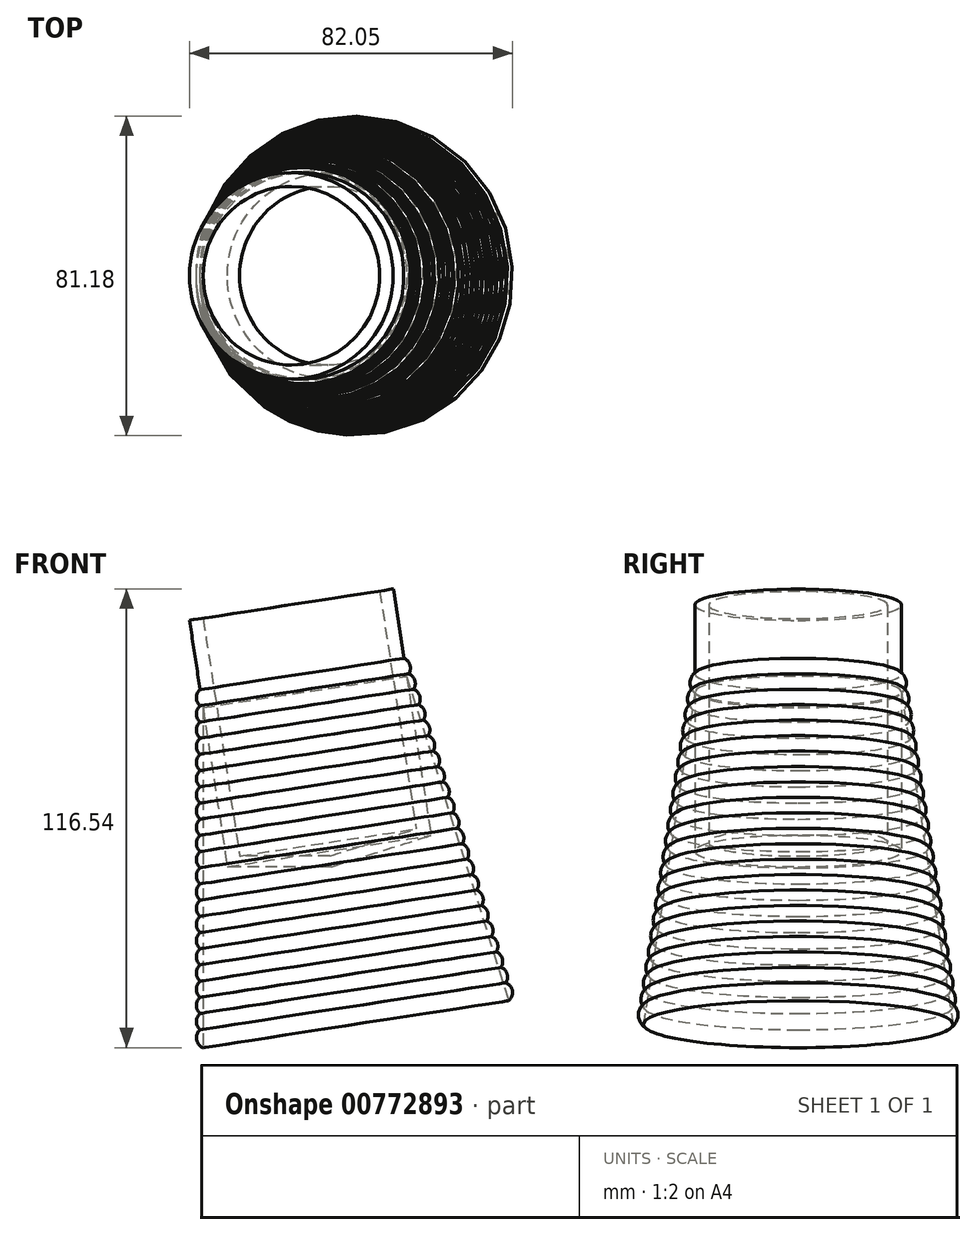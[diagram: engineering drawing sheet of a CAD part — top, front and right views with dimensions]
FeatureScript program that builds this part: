
annotation { "Feature Type Name" : "Feature", "Feature Type Description" : "" }
export const myFeature = defineFeature(function(context is Context, id is Id, definition is map)
    precondition{}
    {
        {
            var Q0;
            Q0=qCreatedBy(makeId("Front.planeOp"),FACE);
            var sketch = newSketch(context, id + "F0", { "sketchPlane" : qUnion([Q0])});
            skLineSegment(sketch, "E0", {"start": v(-26.5, -27.93) * mm, "end": v(-36.1, 34.68) * mm});
            skLineSegment(sketch, "E1", {"start": v(-26.5, -27.93) * mm, "end": v(0, -27.93) * mm});
            skLineSegment(sketch, "E2", {"start": v(0, -27.93) * mm, "end": v(-0.42, -25.21) * mm});
            skLineSegment(sketch, "E3", {"start": v(-0.42, -25.21) * mm, "end": v(-23.38, -25.21) * mm});
            skLineSegment(sketch, "E4", {"start": v(-23.38, -25.21) * mm, "end": v(-32.64, 35.1) * mm});
            skLineSegment(sketch, "E5", {"start": v(-32.64, 35.1) * mm, "end": v(-36.1, 34.68) * mm});
            skArc(sketch, "E6", {"start": v(-33.4, 17.07) * mm, "mid": v(-34.32, 14.6) * mm, "end": v(-32.7, 12.5) * mm});
            skArc(sketch, "E7.0.1.0", {"start": v(-33.4, 12.95) * mm, "mid": v(-34.32, 10.48) * mm, "end": v(-32.7, 8.39) * mm});
            skArc(sketch, "E7.0.2.0", {"start": v(-33.4, 8.84) * mm, "mid": v(-34.32, 6.36) * mm, "end": v(-32.7, 4.27) * mm});
            skArc(sketch, "E7.0.3.0", {"start": v(-33.4, 4.73) * mm, "mid": v(-34.32, 2.25) * mm, "end": v(-32.7, 0.16) * mm});
            skArc(sketch, "E7.0.4.0", {"start": v(-33.4, 0.61) * mm, "mid": v(-34.32, -1.87) * mm, "end": v(-32.7, -3.96) * mm});
            skArc(sketch, "E7.0.5.0", {"start": v(-33.4, -3.5) * mm, "mid": v(-34.32, -5.98) * mm, "end": v(-32.7, -8.07) * mm});
            skArc(sketch, "E7.0.6.0", {"start": v(-33.4, -7.62) * mm, "mid": v(-34.32, -10.1) * mm, "end": v(-32.7, -12.19) * mm});
            skArc(sketch, "E7.0.7.0", {"start": v(-33.4, -11.73) * mm, "mid": v(-34.32, -14.21) * mm, "end": v(-32.7, -16.3) * mm});
            skArc(sketch, "E7.0.8.0", {"start": v(-33.4, -15.85) * mm, "mid": v(-34.32, -18.33) * mm, "end": v(-32.7, -20.42) * mm});
            skArc(sketch, "E7.0.9.0", {"start": v(-33.4, -19.96) * mm, "mid": v(-34.32, -22.44) * mm, "end": v(-32.7, -24.53) * mm});
            skArc(sketch, "E7.0.10.0", {"start": v(-33.4, -24.08) * mm, "mid": v(-34.32, -26.56) * mm, "end": v(-32.7, -28.65) * mm});
            skArc(sketch, "E7.0.11.0", {"start": v(-33.4, -28.2) * mm, "mid": v(-34.32, -30.67) * mm, "end": v(-32.7, -32.76) * mm});
            skArc(sketch, "E7.0.12.0", {"start": v(-33.4, -32.3) * mm, "mid": v(-34.32, -34.79) * mm, "end": v(-32.7, -36.88) * mm});
            skArc(sketch, "E7.0.13.0", {"start": v(-33.4, -36.42) * mm, "mid": v(-34.32, -38.9) * mm, "end": v(-32.7, -41) * mm});
            skArc(sketch, "E7.0.14.0", {"start": v(-33.4, -40.54) * mm, "mid": v(-34.32, -43.02) * mm, "end": v(-32.7, -45.1) * mm});
            skArc(sketch, "E7.0.15.0", {"start": v(-33.4, -44.65) * mm, "mid": v(-34.32, -47.13) * mm, "end": v(-32.7, -49.22) * mm});
            skArc(sketch, "E7.0.16.0", {"start": v(-33.4, -48.77) * mm, "mid": v(-34.32, -51.25) * mm, "end": v(-32.7, -53.34) * mm});
            skArc(sketch, "E7.0.17.0", {"start": v(-33.4, -52.88) * mm, "mid": v(-34.32, -55.36) * mm, "end": v(-32.7, -57.45) * mm});
            skArc(sketch, "E7.0.18.0", {"start": v(-33.4, -57) * mm, "mid": v(-34.32, -59.48) * mm, "end": v(-32.7, -61.56) * mm});
            skArc(sketch, "E7.0.19.0", {"start": v(-33.4, -61.11) * mm, "mid": v(-34.32, -63.6) * mm, "end": v(-32.7, -65.68) * mm});
            skArc(sketch, "E7.0.20.0", {"start": v(-33.4, -65.23) * mm, "mid": v(-34.32, -67.7) * mm, "end": v(-32.7, -69.8) * mm});
            skArc(sketch, "E7.0.21.0", {"start": v(-33.4, -69.34) * mm, "mid": v(-34.32, -71.82) * mm, "end": v(-32.7, -73.9) * mm});
            skLineSegment(sketch, "E7.direction1", {"start": v(-32.7, 12.5) * mm, "end": v(-32.7, 12.5) * mm});
            skLineSegment(sketch, "E7.direction2", {"start": v(-32.7, 12.5) * mm, "end": v(-32.7, 8.39) * mm, "construction": true});
            skLineSegment(sketch, "E8", {"start": v(-32.7, 12.5) * mm, "end": v(-32.7, -73.9) * mm});
            skSolve(sketch);
        }
        {
            var Q0;
            {var subQ0=sQuery(id+"F0.wireOp",EDGE,"E6");var subQ1=sQuery(id+"F0.wireOp",EDGE,"E0");var subQ2=makeQuery(id+"F0.imprint","INTERSECT",VERTEX,{"derivedFrom":[subQ1,subQ0]});Q0=makeQuery(id+"F0.imprint","IMPRINT",FACE,{"disambiguationData":[TD([[makeQuery(id+"F0.imprint","IMPRINT",EDGE,{"disambiguationData":[TD([[subQ2,-1.0]])],"derivedFrom":subQ0}),1.0]])]});}
            var Q1;
            {var subQ1=sQuery(id+"F0.wireOp",EDGE,"E6");var subQ3=sQuery(id+"F0.wireOp",EDGE,"E7.0.1.0");var subQ4=makeQuery(id+"F0.imprint","INTERSECT",VERTEX,{"derivedFrom":[subQ1,subQ3]});Q1=makeQuery(id+"F0.imprint","IMPRINT",FACE,{"disambiguationData":[TD([[makeQuery(id+"F0.imprint","IMPRINT",EDGE,{"disambiguationData":[TD([[subQ4,-1.0]])],"derivedFrom":subQ3}),1.0]])]});}
            var Q2;
            {var subQ0=sQuery(id+"F0.wireOp",EDGE,"E8");var subQ1=sQuery(id+"F0.wireOp",EDGE,"E7.0.1.0");var subQ2=makeQuery(id+"F0.imprint","INTERSECT",VERTEX,{"derivedFrom":[subQ1,subQ0]});Q2=makeQuery(id+"F0.imprint","IMPRINT",FACE,{"disambiguationData":[TD([[makeQuery(id+"F0.imprint","IMPRINT",EDGE,{"disambiguationData":[TD([[subQ2,1.0]])],"derivedFrom":subQ1}),-1.0]])]});}
            var Q3;
            {var subQ0=sQuery(id+"F0.wireOp",EDGE,"E8");var subQ1=sQuery(id+"F0.wireOp",EDGE,"E7.0.2.0");var subQ2=makeQuery(id+"F0.imprint","INTERSECT",VERTEX,{"derivedFrom":[subQ1,subQ0]});Q3=makeQuery(id+"F0.imprint","IMPRINT",FACE,{"disambiguationData":[TD([[makeQuery(id+"F0.imprint","IMPRINT",EDGE,{"disambiguationData":[TD([[subQ2,1.0]])],"derivedFrom":subQ1}),-1.0]])]});}
            var Q4;
            {var subQ0=sQuery(id+"F0.wireOp",EDGE,"E8");var subQ1=sQuery(id+"F0.wireOp",EDGE,"E7.0.3.0");var subQ2=makeQuery(id+"F0.imprint","INTERSECT",VERTEX,{"derivedFrom":[subQ1,subQ0]});Q4=makeQuery(id+"F0.imprint","IMPRINT",FACE,{"disambiguationData":[TD([[makeQuery(id+"F0.imprint","IMPRINT",EDGE,{"disambiguationData":[TD([[subQ2,1.0]])],"derivedFrom":subQ1}),-1.0]])]});}
            var Q5;
            {var subQ0=sQuery(id+"F0.wireOp",EDGE,"E8");var subQ1=sQuery(id+"F0.wireOp",EDGE,"E7.0.4.0");var subQ2=makeQuery(id+"F0.imprint","INTERSECT",VERTEX,{"derivedFrom":[subQ1,subQ0]});Q5=makeQuery(id+"F0.imprint","IMPRINT",FACE,{"disambiguationData":[TD([[makeQuery(id+"F0.imprint","IMPRINT",EDGE,{"disambiguationData":[TD([[subQ2,1.0]])],"derivedFrom":subQ1}),-1.0]])]});}
            var Q6;
            {var subQ0=sQuery(id+"F0.wireOp",EDGE,"E8");var subQ1=sQuery(id+"F0.wireOp",EDGE,"E7.0.5.0");var subQ2=makeQuery(id+"F0.imprint","INTERSECT",VERTEX,{"derivedFrom":[subQ1,subQ0]});Q6=makeQuery(id+"F0.imprint","IMPRINT",FACE,{"disambiguationData":[TD([[makeQuery(id+"F0.imprint","IMPRINT",EDGE,{"disambiguationData":[TD([[subQ2,1.0]])],"derivedFrom":subQ1}),-1.0]])]});}
            var Q7;
            {var subQ0=sQuery(id+"F0.wireOp",EDGE,"E8");var subQ1=sQuery(id+"F0.wireOp",EDGE,"E7.0.6.0");var subQ2=makeQuery(id+"F0.imprint","INTERSECT",VERTEX,{"derivedFrom":[subQ1,subQ0]});Q7=makeQuery(id+"F0.imprint","IMPRINT",FACE,{"disambiguationData":[TD([[makeQuery(id+"F0.imprint","IMPRINT",EDGE,{"disambiguationData":[TD([[subQ2,1.0]])],"derivedFrom":subQ1}),-1.0]])]});}
            var Q8;
            {var subQ0=sQuery(id+"F0.wireOp",EDGE,"E8");var subQ1=sQuery(id+"F0.wireOp",EDGE,"E7.0.7.0");var subQ2=makeQuery(id+"F0.imprint","INTERSECT",VERTEX,{"derivedFrom":[subQ1,subQ0]});Q8=makeQuery(id+"F0.imprint","IMPRINT",FACE,{"disambiguationData":[TD([[makeQuery(id+"F0.imprint","IMPRINT",EDGE,{"disambiguationData":[TD([[subQ2,1.0]])],"derivedFrom":subQ1}),-1.0]])]});}
            var Q9;
            {var subQ0=sQuery(id+"F0.wireOp",EDGE,"E8");var subQ1=sQuery(id+"F0.wireOp",EDGE,"E7.0.8.0");var subQ2=makeQuery(id+"F0.imprint","INTERSECT",VERTEX,{"derivedFrom":[subQ1,subQ0]});Q9=makeQuery(id+"F0.imprint","IMPRINT",FACE,{"disambiguationData":[TD([[makeQuery(id+"F0.imprint","IMPRINT",EDGE,{"disambiguationData":[TD([[subQ2,1.0]])],"derivedFrom":subQ1}),-1.0]])]});}
            var Q10;
            {var subQ0=sQuery(id+"F0.wireOp",EDGE,"E8");var subQ1=sQuery(id+"F0.wireOp",EDGE,"E7.0.9.0");var subQ2=makeQuery(id+"F0.imprint","INTERSECT",VERTEX,{"derivedFrom":[subQ1,subQ0]});Q10=makeQuery(id+"F0.imprint","IMPRINT",FACE,{"disambiguationData":[TD([[makeQuery(id+"F0.imprint","IMPRINT",EDGE,{"disambiguationData":[TD([[subQ2,1.0]])],"derivedFrom":subQ1}),-1.0]])]});}
            var Q11;
            {var subQ0=sQuery(id+"F0.wireOp",EDGE,"E1");Q11=makeQuery(id+"F0.imprint","IMPRINT",FACE,{"disambiguationData":[TD([[makeQuery(id+"F0.imprint","IMPRINT",EDGE,{"derivedFrom":subQ0}),1.0]])]});}
            var Q12;
            {var subQ0=sQuery(id+"F0.wireOp",EDGE,"E8");var subQ1=sQuery(id+"F0.wireOp",EDGE,"E7.0.10.0");var subQ2=makeQuery(id+"F0.imprint","INTERSECT",VERTEX,{"derivedFrom":[subQ1,subQ0]});Q12=makeQuery(id+"F0.imprint","IMPRINT",FACE,{"disambiguationData":[TD([[makeQuery(id+"F0.imprint","IMPRINT",EDGE,{"disambiguationData":[TD([[subQ2,1.0]])],"derivedFrom":subQ1}),-1.0]])]});}
            var Q13;
            {var subQ0=sQuery(id+"F0.wireOp",EDGE,"E8");var subQ1=sQuery(id+"F0.wireOp",EDGE,"E7.0.11.0");var subQ2=makeQuery(id+"F0.imprint","INTERSECT",VERTEX,{"derivedFrom":[subQ1,subQ0]});Q13=makeQuery(id+"F0.imprint","IMPRINT",FACE,{"disambiguationData":[TD([[makeQuery(id+"F0.imprint","IMPRINT",EDGE,{"disambiguationData":[TD([[subQ2,1.0]])],"derivedFrom":subQ1}),-1.0]])]});}
            var Q14;
            {var subQ0=sQuery(id+"F0.wireOp",EDGE,"E8");var subQ1=sQuery(id+"F0.wireOp",EDGE,"E7.0.12.0");var subQ2=makeQuery(id+"F0.imprint","INTERSECT",VERTEX,{"derivedFrom":[subQ1,subQ0]});Q14=makeQuery(id+"F0.imprint","IMPRINT",FACE,{"disambiguationData":[TD([[makeQuery(id+"F0.imprint","IMPRINT",EDGE,{"disambiguationData":[TD([[subQ2,1.0]])],"derivedFrom":subQ1}),-1.0]])]});}
            var Q15;
            {var subQ0=sQuery(id+"F0.wireOp",EDGE,"E8");var subQ1=sQuery(id+"F0.wireOp",EDGE,"E7.0.13.0");var subQ2=makeQuery(id+"F0.imprint","INTERSECT",VERTEX,{"derivedFrom":[subQ1,subQ0]});Q15=makeQuery(id+"F0.imprint","IMPRINT",FACE,{"disambiguationData":[TD([[makeQuery(id+"F0.imprint","IMPRINT",EDGE,{"disambiguationData":[TD([[subQ2,1.0]])],"derivedFrom":subQ1}),-1.0]])]});}
            var Q16;
            {var subQ0=sQuery(id+"F0.wireOp",EDGE,"E8");var subQ1=sQuery(id+"F0.wireOp",EDGE,"E7.0.14.0");var subQ2=makeQuery(id+"F0.imprint","INTERSECT",VERTEX,{"derivedFrom":[subQ1,subQ0]});Q16=makeQuery(id+"F0.imprint","IMPRINT",FACE,{"disambiguationData":[TD([[makeQuery(id+"F0.imprint","IMPRINT",EDGE,{"disambiguationData":[TD([[subQ2,1.0]])],"derivedFrom":subQ1}),-1.0]])]});}
            var Q17;
            {var subQ0=sQuery(id+"F0.wireOp",EDGE,"E8");var subQ1=sQuery(id+"F0.wireOp",EDGE,"E7.0.15.0");var subQ2=makeQuery(id+"F0.imprint","INTERSECT",VERTEX,{"derivedFrom":[subQ1,subQ0]});Q17=makeQuery(id+"F0.imprint","IMPRINT",FACE,{"disambiguationData":[TD([[makeQuery(id+"F0.imprint","IMPRINT",EDGE,{"disambiguationData":[TD([[subQ2,1.0]])],"derivedFrom":subQ1}),-1.0]])]});}
            var Q18;
            {var subQ0=sQuery(id+"F0.wireOp",EDGE,"E8");var subQ1=sQuery(id+"F0.wireOp",EDGE,"E7.0.16.0");var subQ2=makeQuery(id+"F0.imprint","INTERSECT",VERTEX,{"derivedFrom":[subQ1,subQ0]});Q18=makeQuery(id+"F0.imprint","IMPRINT",FACE,{"disambiguationData":[TD([[makeQuery(id+"F0.imprint","IMPRINT",EDGE,{"disambiguationData":[TD([[subQ2,1.0]])],"derivedFrom":subQ1}),-1.0]])]});}
            var Q19;
            {var subQ0=sQuery(id+"F0.wireOp",EDGE,"E8");var subQ1=sQuery(id+"F0.wireOp",EDGE,"E7.0.17.0");var subQ2=makeQuery(id+"F0.imprint","INTERSECT",VERTEX,{"derivedFrom":[subQ1,subQ0]});Q19=makeQuery(id+"F0.imprint","IMPRINT",FACE,{"disambiguationData":[TD([[makeQuery(id+"F0.imprint","IMPRINT",EDGE,{"disambiguationData":[TD([[subQ2,1.0]])],"derivedFrom":subQ1}),-1.0]])]});}
            var Q20;
            {var subQ0=sQuery(id+"F0.wireOp",EDGE,"E8");var subQ1=sQuery(id+"F0.wireOp",EDGE,"E7.0.18.0");var subQ2=makeQuery(id+"F0.imprint","INTERSECT",VERTEX,{"derivedFrom":[subQ1,subQ0]});Q20=makeQuery(id+"F0.imprint","IMPRINT",FACE,{"disambiguationData":[TD([[makeQuery(id+"F0.imprint","IMPRINT",EDGE,{"disambiguationData":[TD([[subQ2,1.0]])],"derivedFrom":subQ1}),-1.0]])]});}
            var Q21;
            {var subQ0=sQuery(id+"F0.wireOp",EDGE,"E8");var subQ1=sQuery(id+"F0.wireOp",EDGE,"E7.0.19.0");var subQ2=makeQuery(id+"F0.imprint","INTERSECT",VERTEX,{"derivedFrom":[subQ1,subQ0]});Q21=makeQuery(id+"F0.imprint","IMPRINT",FACE,{"disambiguationData":[TD([[makeQuery(id+"F0.imprint","IMPRINT",EDGE,{"disambiguationData":[TD([[subQ2,1.0]])],"derivedFrom":subQ1}),-1.0]])]});}
            var Q22;
            {var subQ0=sQuery(id+"F0.wireOp",EDGE,"E8");var subQ1=sQuery(id+"F0.wireOp",EDGE,"E7.0.20.0");var subQ2=makeQuery(id+"F0.imprint","INTERSECT",VERTEX,{"derivedFrom":[subQ1,subQ0]});Q22=makeQuery(id+"F0.imprint","IMPRINT",FACE,{"disambiguationData":[TD([[makeQuery(id+"F0.imprint","IMPRINT",EDGE,{"disambiguationData":[TD([[subQ2,1.0]])],"derivedFrom":subQ1}),-1.0]])]});}
            var Q23;
            Q23=sQuery(id+"F0.wireOp",EDGE,"E2");
            revolve(context, id + "F1", {"surfaceOperationType" : NewSurfaceOperationType.NEW, "entities" : qUnion([Q0, Q1, Q2, Q3, Q4, Q5, Q6, Q7, Q8, Q9, Q10, Q11, Q12, Q13, Q14, Q15, Q16, Q17, Q18, Q19, Q20, Q21, Q22]), "axis" : qUnion([Q23]), "revolveType" : RevolveType.FULL});
        }
    });
